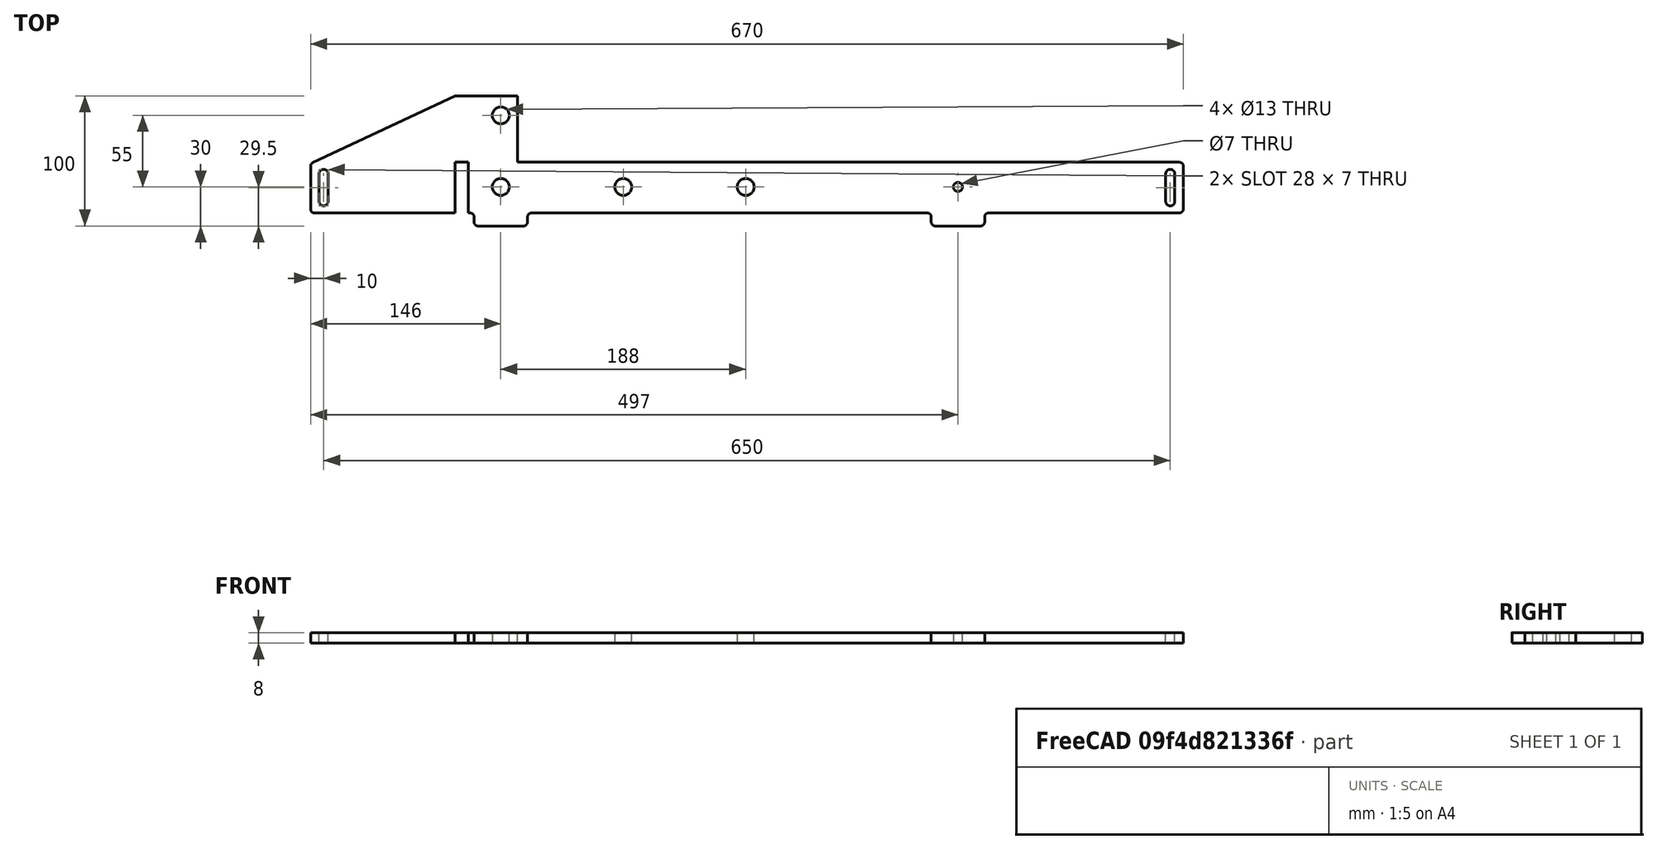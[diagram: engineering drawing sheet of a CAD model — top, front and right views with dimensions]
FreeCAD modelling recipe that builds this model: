
FCSTD DOCUMENT  (FreeCAD 0.19R24366 (Git))
Label: Front back feet plates
License: All rights reserved
LicenseURL: http://en.wikipedia.org/wiki/All_rights_reserved
objects: Sketcher::SketchObject×1, PartDesign::Pad×1, PartDesign::Body×1
note: 4 computed .brp shape members not serialized (recipe doc carries the construction recipe); baked Part::Feature solids carry a one-line shape summary decoded from their .brp

FEATURE [Sketcher::SketchObject] Sketch
  FullyConstrained = true
  MapMode = 5
  Support = -> [XY_Plane]
  sketch-geometry (73):
    g0: Circle CenterX=-24 CenterY=35 CenterZ=0 NormalX=0 NormalY=0 NormalZ=1 AngleXU=0 Radius=6.5
    g1: Circle CenterX=-24 CenterY=-20 CenterZ=0 NormalX=0 NormalY=0 NormalZ=1 AngleXU=0 Radius=6.5
    g2: LineSegment StartX=-11 StartY=50 StartZ=0 EndX=-11 EndY=-1 EndZ=0
    g3: LineSegment StartX=-11 StartY=-1 StartZ=0 EndX=497 EndY=-1 EndZ=0
    g4: Circle CenterX=164 CenterY=-20 CenterZ=0 NormalX=0 NormalY=0 NormalZ=1 AngleXU=0 Radius=6.5
    g5: ArcOfCircle CenterX=490 CenterY=-10 CenterZ=0 NormalX=0 NormalY=0 NormalZ=1 AngleXU=0 Radius=3.5 StartAngle=2e-16 EndAngle=3.14159
    g6: ArcOfCircle CenterX=490 CenterY=-31 CenterZ=0 NormalX=0 NormalY=0 NormalZ=1 AngleXU=0 Radius=3.5 StartAngle=3.14159 EndAngle=6.28319
    g7: LineSegment StartX=486.5 StartY=-10 StartZ=0 EndX=486.5 EndY=-31 EndZ=0
    g8: LineSegment StartX=493.5 StartY=-10 StartZ=0 EndX=493.5 EndY=-31 EndZ=0
    g9: LineSegment StartX=500 StartY=-4 StartZ=0 EndX=500 EndY=-37 EndZ=0
    g10: ArcOfCircle CenterX=497 CenterY=-4 CenterZ=0 NormalX=0 NormalY=0 NormalZ=1 AngleXU=0 Radius=3 StartAngle=0 EndAngle=1.5708
    g11: ArcOfCircle CenterX=497 CenterY=-37 CenterZ=0 NormalX=0 NormalY=0 NormalZ=1 AngleXU=0 Radius=3 StartAngle=4.71239 EndAngle=6.28319
    g12: LineSegment StartX=-24 StartY=-20 StartZ=0 EndX=164 EndY=-20 EndZ=0
    g13: Circle CenterX=70 CenterY=-20 CenterZ=0 NormalX=0 NormalY=0 NormalZ=1 AngleXU=0 Radius=6.5
    g14: LineSegment StartX=309.5 StartY=-50 StartZ=0 EndX=344.5 EndY=-50 EndZ=0
    g15: LineSegment StartX=-41.5 StartY=-50 StartZ=0 EndX=-6.5 EndY=-50 EndZ=0
    g16: LineSegment StartX=-24 StartY=-20 StartZ=0 EndX=-24 EndY=-50 EndZ=0
    g17: LineSegment StartX=306.5 StartY=-47 StartZ=0 EndX=306.5 EndY=-43 EndZ=0
    g18: LineSegment StartX=347.5 StartY=-47 StartZ=0 EndX=347.5 EndY=-43 EndZ=0
    g19: LineSegment StartX=350.5 StartY=-40 StartZ=0 EndX=497 EndY=-40 EndZ=0
    g20: ArcOfCircle CenterX=303.5 CenterY=-43 CenterZ=0 NormalX=0 NormalY=0 NormalZ=1 AngleXU=0 Radius=3 StartAngle=-9e-16 EndAngle=1.5708
    g21: ArcOfCircle CenterX=309.5 CenterY=-47 CenterZ=0 NormalX=0 NormalY=0 NormalZ=1 AngleXU=0 Radius=3 StartAngle=3.14159 EndAngle=4.71239
    g22: ArcOfCircle CenterX=344.5 CenterY=-47 CenterZ=0 NormalX=0 NormalY=0 NormalZ=1 AngleXU=0 Radius=3 StartAngle=4.71239 EndAngle=6.28319
    g23: ArcOfCircle CenterX=350.5 CenterY=-43 CenterZ=0 NormalX=0 NormalY=0 NormalZ=1 AngleXU=0 Radius=3 StartAngle=1.5708 EndAngle=3.14159
    g24: LineSegment StartX=303.5 StartY=-40 StartZ=0 EndX=350.5 EndY=-40 EndZ=0
    g25: LineSegment StartX=-47.5 StartY=-40 StartZ=0 EndX=-0.5 EndY=-40 EndZ=0
    g26: LineSegment StartX=-44.5 StartY=-43 StartZ=0 EndX=-44.5 EndY=-47 EndZ=0
    g27: LineSegment StartX=-3.5 StartY=-47 StartZ=0 EndX=-3.5 EndY=-43 EndZ=0
    g28: ArcOfCircle CenterX=-47.5 CenterY=-43 CenterZ=0 NormalX=0 NormalY=0 NormalZ=1 AngleXU=0 Radius=3 StartAngle=0 EndAngle=1.5708
    g29: ArcOfCircle CenterX=-41.5 CenterY=-47 CenterZ=0 NormalX=0 NormalY=0 NormalZ=1 AngleXU=0 Radius=3 StartAngle=3.14159 EndAngle=4.71239
    g30: ArcOfCircle CenterX=-6.5 CenterY=-47 CenterZ=0 NormalX=0 NormalY=0 NormalZ=1 AngleXU=0 Radius=3 StartAngle=4.71239 EndAngle=6.28319
    g31: ArcOfCircle CenterX=-0.5 CenterY=-43 CenterZ=0 NormalX=0 NormalY=0 NormalZ=1 AngleXU=0 Radius=3 StartAngle=1.5708 EndAngle=3.14159
    g32: LineSegment StartX=309.5 StartY=-50 StartZ=0 EndX=-6.5 EndY=-50 EndZ=0
    g33: LineSegment StartX=-0.5 StartY=-40 StartZ=0 EndX=303.5 EndY=-40 EndZ=0
    g34: GeomPoint X=-24 Y=-40 Z=0
    g35: LineSegment StartX=164 StartY=-20 StartZ=0 EndX=490 EndY=-20 EndZ=0
    g36: LineSegment StartX=490 StartY=-10 StartZ=0 EndX=490 EndY=-31 EndZ=0
    g37: Circle CenterX=327 CenterY=-20 CenterZ=0 NormalX=0 NormalY=0 NormalZ=1 AngleXU=0 Radius=3.5
    g38: ArcOfCircle CenterX=-160 CenterY=-31 CenterZ=0 NormalX=0 NormalY=0 NormalZ=1 AngleXU=0 Radius=3.5 StartAngle=3.14159 EndAngle=6.28319
    g39: ArcOfCircle CenterX=-160 CenterY=-10 CenterZ=0 NormalX=0 NormalY=0 NormalZ=1 AngleXU=0 Radius=3.5 StartAngle=0 EndAngle=3.14159
    g40: LineSegment StartX=-156.5 StartY=-31 StartZ=0 EndX=-156.5 EndY=-10 EndZ=0
    g41: LineSegment StartX=-163.5 StartY=-31 StartZ=0 EndX=-163.5 EndY=-10 EndZ=0
    g42: LineSegment StartX=-168.275 StartY=-1.28421 StartZ=0 EndX=-59 EndY=50 EndZ=0
    g43: LineSegment StartX=-170 StartY=-4 StartZ=0 EndX=-170 EndY=-37 EndZ=0
    g44: ArcOfCircle CenterX=-167 CenterY=-37 CenterZ=0 NormalX=0 NormalY=0 NormalZ=1 AngleXU=0 Radius=3 StartAngle=3.14159 EndAngle=4.71239
    g45: ArcOfCircle CenterX=-167 CenterY=-4 CenterZ=0 NormalX=0 NormalY=0 NormalZ=1 AngleXU=0 Radius=3 StartAngle=2.0096 EndAngle=3.14159
    g46: LineSegment StartX=-49 StartY=50 StartZ=0 EndX=-11 EndY=50 EndZ=0
    g47: LineSegment StartX=-49 StartY=50 StartZ=0 EndX=-49 EndY=-1 EndZ=0
    g48: LineSegment StartX=-59 StartY=-1 StartZ=0 EndX=-59 EndY=50 EndZ=0
    g49: LineSegment StartX=-59 StartY=50 StartZ=0 EndX=-58 EndY=50 EndZ=0
    g50: LineSegment StartX=-58 StartY=50 StartZ=0 EndX=-54 EndY=50 EndZ=0
    g51: LineSegment StartX=-54 StartY=50 StartZ=0 EndX=-50 EndY=50 EndZ=0
    g52: LineSegment StartX=-50 StartY=50 StartZ=0 EndX=-49 EndY=50 EndZ=0
    g53: LineSegment StartX=-54 StartY=50 StartZ=0 EndX=-54 EndY=-40 EndZ=0
    g54: LineSegment StartX=-50 StartY=50 StartZ=0 EndX=-50 EndY=-40 EndZ=0
    g55: LineSegment StartX=-58 StartY=50 StartZ=0 EndX=-58 EndY=-40 EndZ=0
    g56: LineSegment StartX=-24 StartY=35 StartZ=0 EndX=-24 EndY=-20 EndZ=0
    g57: GeomPoint X=327 Y=-50 Z=0
    g58: LineSegment StartX=327 StartY=-50 StartZ=0 EndX=327 EndY=-20 EndZ=0
    g59: LineSegment StartX=-59 StartY=-1 StartZ=0 EndX=-59 EndY=-40 EndZ=0
    g60: LineSegment StartX=-49 StartY=-1 StartZ=0 EndX=-49 EndY=-40 EndZ=0
    g61: LineSegment StartX=-167 StartY=-40 StartZ=0 EndX=-59 EndY=-40 EndZ=0
    g62: LineSegment StartX=-59 StartY=-40 StartZ=0 EndX=-58 EndY=-40 EndZ=0
    g63: LineSegment StartX=-58 StartY=-40 StartZ=0 EndX=-54 EndY=-40 EndZ=0
    g64: LineSegment StartX=-54 StartY=-40 StartZ=0 EndX=-50 EndY=-40 EndZ=0
    g65: LineSegment StartX=-50 StartY=-40 StartZ=0 EndX=-49 EndY=-40 EndZ=0
    g66: LineSegment StartX=-49 StartY=-40 StartZ=0 EndX=-47.5 EndY=-40 EndZ=0
    g67: LineSegment StartX=-59 StartY=-1 StartZ=0 EndX=-58 EndY=-1 EndZ=0
    g68: LineSegment StartX=-58 StartY=-1 StartZ=0 EndX=-54 EndY=-1 EndZ=0
    g69: LineSegment StartX=-54 StartY=-1 StartZ=0 EndX=-50 EndY=-1 EndZ=0
    g70: LineSegment StartX=-50 StartY=-1 StartZ=0 EndX=-49 EndY=-1 EndZ=0
    g71: LineSegment StartX=-49 StartY=-1 StartZ=0 EndX=-11 EndY=-1 EndZ=0
    g72: LineSegment StartX=500 StartY=-4 StartZ=0 EndX=-170 EndY=-4 EndZ=0
  constraints (184):
    c: DistanceY(g-1,g0) = 35
    c: DistanceX(g0,g-1) = 24
    c: Radius(g0) = 6.5
    c: Vertical(g2)
    c: DistanceX(g2,g-1) = 11
    c: Horizontal(g3)
    c: DistanceX(g1,g4) = 188
    c: Equal(g1,g4)
    c: Tangent(g5,g8) = 1.5708
    c: Tangent(g5,g7) = -1.5708
    c: Tangent(g7,g6) = -1.5708
    c: Tangent(g8,g6) = 1.5708
    c: Vertical(g7)
    c: Equal(g5,g6)
    c: Vertical(g9)
    c: Radius(g5) = 3.5
    c: Tangent(g3,g10) = 1.5708
    c: Tangent(g9,g10) = 1.5708
    c: Tangent(g9,g11) = 1.5708
    c: DistanceY(g5,g3) = 9
    c: DistanceY(g19,g6) = 9
    c: Radius(g10) = 3
    c: DistanceX(g6,g9) = 10
    c: Equal(g11,g10)
    c: Coincident(g12,g1)
    c: Coincident(g12,g4)
    c: Horizontal(g12)
    c: Symmetric(g1,g4,g13)
    c: Equal(g13,g1)
    c: Horizontal(g14)
    c: Horizontal(g15)
    c: Coincident(g16,g1)
    c: Vertical(g16)
    c: Vertical(g18)
    c: Vertical(g17)
    c: Tangent(g17,g20) = -1.5708
    c: Coincident(g24,g20) = 1.5708
    c: Tangent(g17,g21) = 1.5708
    c: Tangent(g14,g21) = -1.5708
    c: Tangent(g18,g22) = -1.5708
    c: Tangent(g14,g22) = -1.5708
    c: Tangent(g18,g23) = 1.5708
    c: Tangent(g19,g23) = 1.5708
    c: Coincident(g24,g19)
    c: Coincident(g25,g28) = -1.5708
    c: Tangent(g26,g28) = 1.5708
    c: Tangent(g26,g29) = -1.5708
    c: Tangent(g15,g29) = -1.5708
    c: Tangent(g27,g30) = -1.5708
    c: Tangent(g15,g30) = -1.5708
    c: Tangent(g27,g31) = 1.5708
    c: Coincident(g25,g31) = -1.5708
    c: Vertical(g26)
    c: Vertical(g27)
    c: Equal(g28,g29)
    c: Equal(g29,g30)
    c: Equal(g30,g31)
    c: Equal(g31,g20)
    c: Equal(g20,g21)
    c: Equal(g21,g22)
    c: Equal(g22,g23)
    c: Symmetric(g15,g15,g16)
    c: Coincident(g32,g14)
    c: Coincident(g32,g15)
    c: Horizontal(g32)
    c: Equal(g15,g14)
    c: DistanceY(g15,g25) = 10
    c: Radius(g30) = 3
    c: Horizontal(g33)
    c: DistanceX(g15,g15) = 35
    c: Tangent(g33,g20) = 1.5708
    c: Horizontal(g24)
    c: Horizontal(g25)
    c: Tangent(g33,g31) = 1.5708
    c: Horizontal(g19)
    c: Radius(g4) = 6.5
    c: PointOnObject(g34,g25)
    c: PointOnObject(g34,g16)
    c: DistanceY(g34,g1) = 20
    c: DistanceY(g3,g-1) = 1
    c: DistanceX(g-1,g6) = 490
    c: Tangent(g19,g11) = -1.5708
    c: DistanceY(g13,g-1) = 20
    c: Coincident(g35,g4)
    c: Horizontal(g35)
    c: Coincident(g36,g5)
    c: Coincident(g36,g6)
    c: PointOnObject(g35,g36)
    c: Symmetric(g4,g35,g37)
    c: Equal(g37,g5)
    c: Coincident(g3,g2)
    c: Tangent(g38,g41) = 1.5708
    c: Tangent(g38,g40) = -1.5708
    c: Tangent(g40,g39) = -1.5708
    c: Tangent(g41,g39) = 1.5708
    c: Vertical(g40)
    c: Equal(g38,g39)
    c: Equal(g5,g39)
    c: DistanceX(g38,g-1) = 160
    c: Vertical(g43)
    c: Tangent(g42,g45) = 1.5708
    c: Tangent(g43,g45) = -1.5708
    c: Equal(g44,g45)
    c: Equal(g45,g10)
    c: DistanceX(g43,g38) = 10
    c: Coincident(g46,g2)
    c: Horizontal(g46)
    c: Vertical(g47)
    c: Vertical(g48)
    c: Coincident(g48,g42)
    c: DistanceX(g42,g46) = 10
    c: Coincident(g49,g42)
    c: Coincident(g50,g49)
    c: Horizontal(g50)
    c: Coincident(g51,g50)
    c: Coincident(g52,g51)
    c: Coincident(g52,g46)
    c: Coincident(g53,g50)
    c: Vertical(g53)
    c: Coincident(g54,g51)
    c: Vertical(g54)
    c: Coincident(g55,g49)
    c: Vertical(g55)
    c: Horizontal(g49)
    c: Symmetric(g49,g51,g50)
    c: Symmetric(g42,g46,g50)
    c: DistanceX(g49,g51) = 8
    c: Coincident(g47,g46)
    c: DistanceX(g51,g-1) = 50
    c: DistanceY(g-1,g2) = 50
    c: Coincident(g56,g0)
    c: Coincident(g56,g1)
    c: Vertical(g56)
    c: DistanceY(g55,g48) = 39
    c: DistanceY(g11,g3) = 39
    c: Symmetric(g14,g14,g57)
    c: Coincident(g58,g57)
    c: Coincident(g58,g37)
    c: Vertical(g58)
    c: Coincident(g59,g48)
    c: Vertical(g59)
    c: Coincident(g60,g47)
    c: Vertical(g60)
    c: Coincident(g61,g59)
    c: Horizontal(g61)
    c: Coincident(g62,g59)
    c: Coincident(g62,g55)
    c: Horizontal(g62)
    c: Coincident(g63,g62)
    c: Coincident(g63,g53)
    c: Horizontal(g63)
    c: Coincident(g64,g63)
    c: Coincident(g64,g54)
    c: Horizontal(g64)
    c: Coincident(g65,g64)
    c: Coincident(g65,g60)
    c: Horizontal(g65)
    c: Coincident(g66,g60)
    c: Horizontal(g66)
    c: Tangent(g66,g28) = 1.5708
    c: Tangent(g61,g44) = -1.5708
    c: DistanceY(g11,g9) = 36
    c: DistanceY(g44,g38) = 9
    c: DistanceY(g8,g8) = 21
    c: DistanceY(g41,g41) = 21
    c: Tangent(g44,g43) = -1.5708
    c: Coincident(g67,g59)
    c: PointOnObject(g67,g55)
    c: Horizontal(g67)
    c: Coincident(g68,g67)
    c: PointOnObject(g68,g53)
    c: Horizontal(g68)
    c: Coincident(g69,g68)
    c: PointOnObject(g69,g54)
    c: Horizontal(g69)
    c: Coincident(g70,g69)
    c: Coincident(g70,g60)
    c: Horizontal(g70)
    c: Coincident(g71,g60)
    c: Coincident(g71,g2)
    c: Horizontal(g71)
    c: Coincident(g72,g9)
    c: Coincident(g72,g43)
    c: Horizontal(g72)
FEATURE [PartDesign::Pad] Pad  label="Plate thickness pad"
  Direction = (1,1,1)
  Length = 8
  Length2 = 100
  Profile = -> Sketch
  Type = 0
FEATURE [PartDesign::Body] Body
  Group = -> [Sketch,Pad]
  Origin = -> Origin
  Tip = -> Pad
